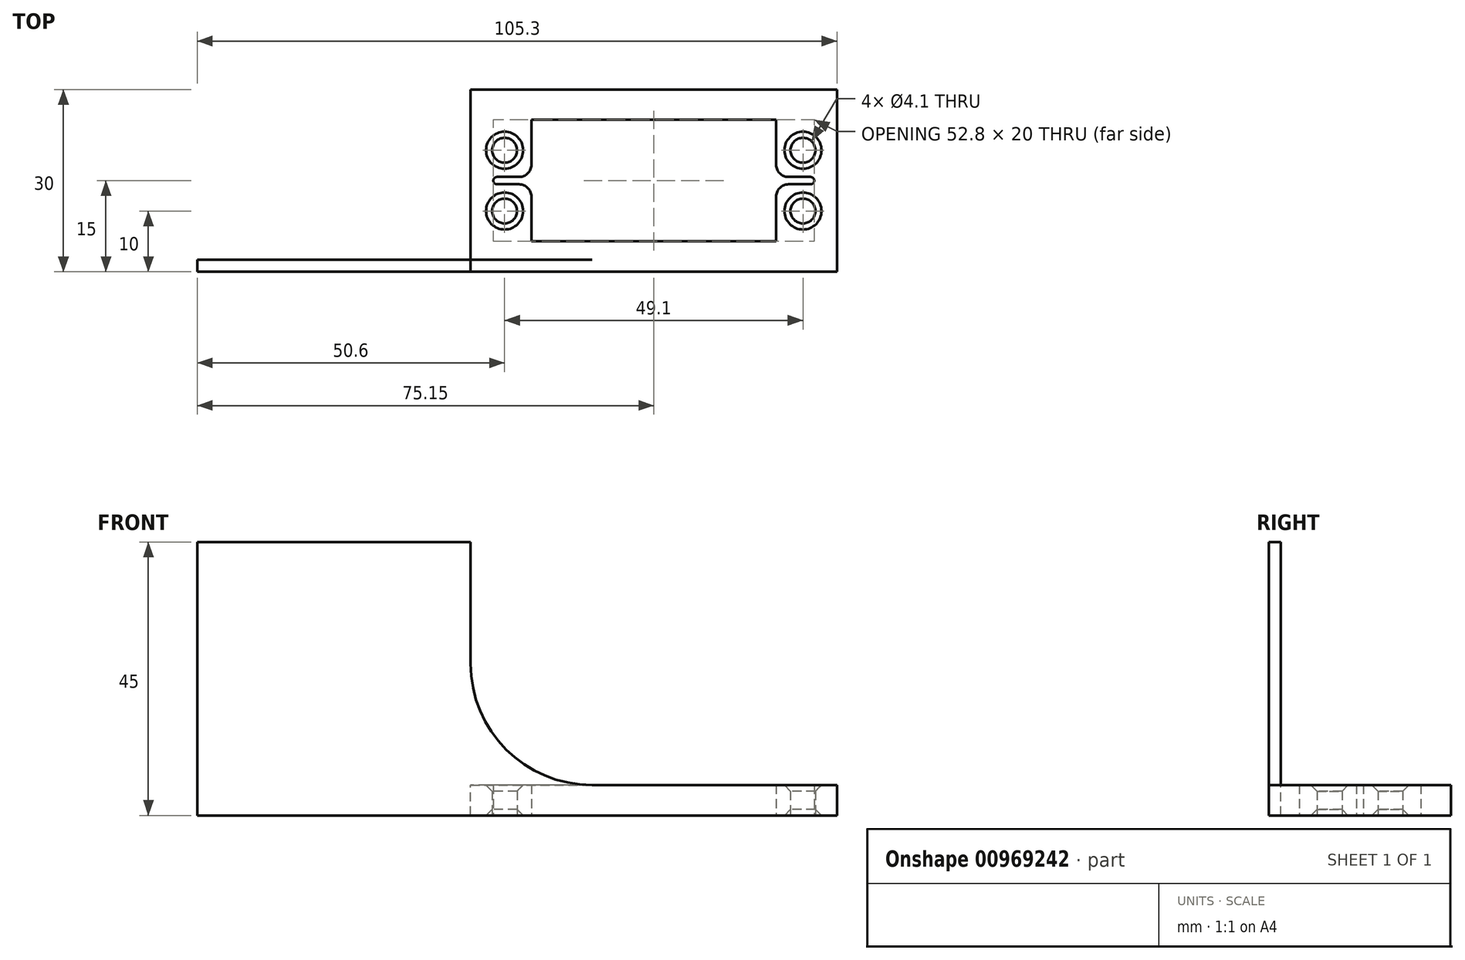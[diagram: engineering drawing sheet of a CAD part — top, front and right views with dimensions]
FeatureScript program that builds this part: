
annotation { "Feature Type Name" : "Feature", "Feature Type Description" : "" }
export const myFeature = defineFeature(function(context is Context, id is Id, definition is map)
    precondition{}
    {
        {
            var Q0;
            Q0=qCreatedBy(makeId("Top.planeOp"),FACE);
            var sketch = newSketch(context, id + "F0", { "sketchPlane" : qUnion([Q0])});
            skLineSegment(sketch, "E0.bottom", {"start": v(30.15, -15) * mm, "end": v(-30.15, -15) * mm});
            skLineSegment(sketch, "E0.top", {"start": v(30.15, 15) * mm, "end": v(-30.15, 15) * mm});
            skLineSegment(sketch, "E0.left", {"start": v(30.15, -15) * mm, "end": v(30.15, 15) * mm});
            skLineSegment(sketch, "E0.right", {"start": v(-30.15, -15) * mm, "end": v(-30.15, 15) * mm});
            skPoint(sketch, "E0.middle", {"position": v(0, 0) * mm});
            skLineSegment(sketch, "E1", {"start": v(0, 10) * mm, "end": v(20.15, 10) * mm});
            skLineSegment(sketch, "E2", {"start": v(20.15, 10) * mm, "end": v(20.15, 2.6) * mm});
            skLineSegment(sketch, "E3", {"start": v(22.15, 0.6) * mm, "end": v(25.8, 0.6) * mm});
            skLineSegment(sketch, "E4", {"start": v(26.4, 0) * mm, "end": v(26.4, 0) * mm});
            skPoint(sketch, "E5.visualSharp", {"position": v(26.4, 0.6) * mm});
            skArc(sketch, "E5.filletArc", {"start": v(26.4, 0) * mm, "mid": v(26.22, 0.42) * mm, "end": v(25.8, 0.6) * mm});
            skPoint(sketch, "E6.visualSharp", {"position": v(20.15, 0.6) * mm});
            skArc(sketch, "E6.filletArc", {"start": v(20.15, 2.6) * mm, "mid": v(20.74, 1.19) * mm, "end": v(22.15, 0.6) * mm});
            skCircle(sketch, "E7", {"center": v(24.55, 5) * mm, "radius": 2.05 * mm});
            skLineSegment(sketch, "E8.MirrorCS", {"start": v(0, 10) * mm, "end": v(-20.15, 10) * mm});
            skArc(sketch, "E9.MirrorCS", {"start": v(-26.4, 0) * mm, "mid": v(-26.22, 0.42) * mm, "end": v(-25.8, 0.6) * mm});
            skArc(sketch, "E10.MirrorCS", {"start": v(-20.15, 2.6) * mm, "mid": v(-20.74, 1.19) * mm, "end": v(-22.15, 0.6) * mm});
            skPoint(sketch, "E11.MirrorP", {"position": v(-26.4, 0.6) * mm});
            skLineSegment(sketch, "E12.MirrorCS", {"start": v(-20.15, 10) * mm, "end": v(-20.15, 2.6) * mm});
            skLineSegment(sketch, "E13.MirrorCS", {"start": v(-26.4, 0) * mm, "end": v(-26.4, 0) * mm});
            skCircle(sketch, "E14.MirrorC", {"center": v(-24.55, 5) * mm, "radius": 2.05 * mm});
            skLineSegment(sketch, "E15.MirrorCS", {"start": v(-22.15, 0.6) * mm, "end": v(-25.8, 0.6) * mm});
            skPoint(sketch, "E16.MirrorP", {"position": v(-20.15, 0.6) * mm});
            skArc(sketch, "E17.MirrorCS", {"start": v(-26.4, 0) * mm, "mid": v(-26.22, -0.42) * mm, "end": v(-25.8, -0.6) * mm});
            skArc(sketch, "E18.MirrorCS", {"start": v(26.4, 0) * mm, "mid": v(26.22, -0.42) * mm, "end": v(25.8, -0.6) * mm});
            skArc(sketch, "E19.MirrorCS", {"start": v(-20.15, -2.6) * mm, "mid": v(-20.74, -1.19) * mm, "end": v(-22.15, -0.6) * mm});
            skLineSegment(sketch, "E20.MirrorCS", {"start": v(0, -10) * mm, "end": v(-20.15, -10) * mm});
            skArc(sketch, "E21.MirrorCS", {"start": v(20.15, -2.6) * mm, "mid": v(20.74, -1.19) * mm, "end": v(22.15, -0.6) * mm});
            skLineSegment(sketch, "E22.MirrorCS", {"start": v(-20.15, -10) * mm, "end": v(-20.15, -2.6) * mm});
            skLineSegment(sketch, "E23.MirrorCS", {"start": v(-22.15, -0.6) * mm, "end": v(-25.8, -0.6) * mm});
            skCircle(sketch, "E24.MirrorC", {"center": v(-24.55, -5) * mm, "radius": 2.05 * mm});
            skPoint(sketch, "E25.MirrorP", {"position": v(26.4, -0.6) * mm});
            skCircle(sketch, "E26.MirrorC", {"center": v(24.55, -5) * mm, "radius": 2.05 * mm});
            skPoint(sketch, "E27.MirrorP", {"position": v(20.15, -0.6) * mm});
            skLineSegment(sketch, "E28.MirrorCS", {"start": v(0, -10) * mm, "end": v(20.15, -10) * mm});
            skLineSegment(sketch, "E29.MirrorCS", {"start": v(22.15, -0.6) * mm, "end": v(25.8, -0.6) * mm});
            skPoint(sketch, "E30.MirrorP", {"position": v(-26.4, -0.6) * mm});
            skLineSegment(sketch, "E31.MirrorCS", {"start": v(20.15, -10) * mm, "end": v(20.15, -2.6) * mm});
            skPoint(sketch, "E32.MirrorP", {"position": v(-20.15, -0.6) * mm});
            skSolve(sketch);
        }
        {
            var Q0;
            Q0 = qSketchRegion(id + "F0", true);
            extrude(context, id + "F1", {"entities" : qUnion([Q0]), "depth" : 5 * mm, "offsetDistance" : 25 * mm});
        }
        {
            var Q0;
            Q0=makeQuery(id+"F1.opExtrude","SWEPT_FACE",FACE,{"disambiguationData":[OSD([sQuery(id+"F0.wireOp",EDGE,"E0.bottom")])]});
            var sketch = newSketch(context, id + "F2", { "sketchPlane" : qUnion([Q0])});
            skLineSegment(sketch, "E33", {"start": v(-12.9, 0) * mm, "end": v(-75.15, 0) * mm});
            skLineSegment(sketch, "E34", {"start": v(-75.15, 0) * mm, "end": v(-75.15, 45) * mm});
            skLineSegment(sketch, "E35", {"start": v(-75.15, 45) * mm, "end": v(-30.15, 45) * mm});
            skLineSegment(sketch, "E36", {"start": v(-30.15, 45) * mm, "end": v(-30.15, 25) * mm});
            skLineSegment(sketch, "E37", {"start": v(-12.9, 5) * mm, "end": v(-10.15, 5) * mm});
            skLineSegment(sketch, "E38", {"start": v(-12.9, 5) * mm, "end": v(-12.9, 0) * mm});
            skPoint(sketch, "E39.visualSharp", {"position": v(-30.15, 5) * mm});
            skArc(sketch, "E39.filletArc", {"start": v(-30.15, 25) * mm, "mid": v(-24.3, 10.86) * mm, "end": v(-10.15, 5) * mm});
            skSolve(sketch);
        }
        {
            var Q0;
            Q0 = qSketchRegion(id + "F2", true);
            extrude(context, id + "F3", {"entities" : qUnion([Q0]), "operationType" : NewBodyOperationType.ADD, "oppositeDirection" : true, "depth" : 2 * mm, "offsetDistance" : 25 * mm});
        }
        {
            var Q0;
            Q0=makeQuery(id+"F1.opExtrude","CAP_EDGE",EDGE,{"disambiguationData":[OSD([sQuery(id+"F0.wireOp",EDGE,"E14.MirrorC")])],"isStart":false});
            var Q1;
            Q1=makeQuery(id+"F1.opExtrude","SWEPT_FACE",FACE,{"disambiguationData":[OSD([sQuery(id+"F0.wireOp",EDGE,"E24.MirrorC")])]});
            var Q2;
            Q2=makeQuery(id+"F1.opExtrude","SWEPT_FACE",FACE,{"disambiguationData":[OSD([sQuery(id+"F0.wireOp",EDGE,"E7")])]});
            var Q3;
            Q3=makeQuery(id+"F1.opExtrude","CAP_EDGE",EDGE,{"disambiguationData":[OSD([sQuery(id+"F0.wireOp",EDGE,"E26.MirrorC")])],"isStart":false});
            chamfer(context, id + "F4", {"entities" : qUnion([Q0, Q1, Q2, Q3]), "width" : 1 * mm, "tangentPropagation" : true});
        }
    });
